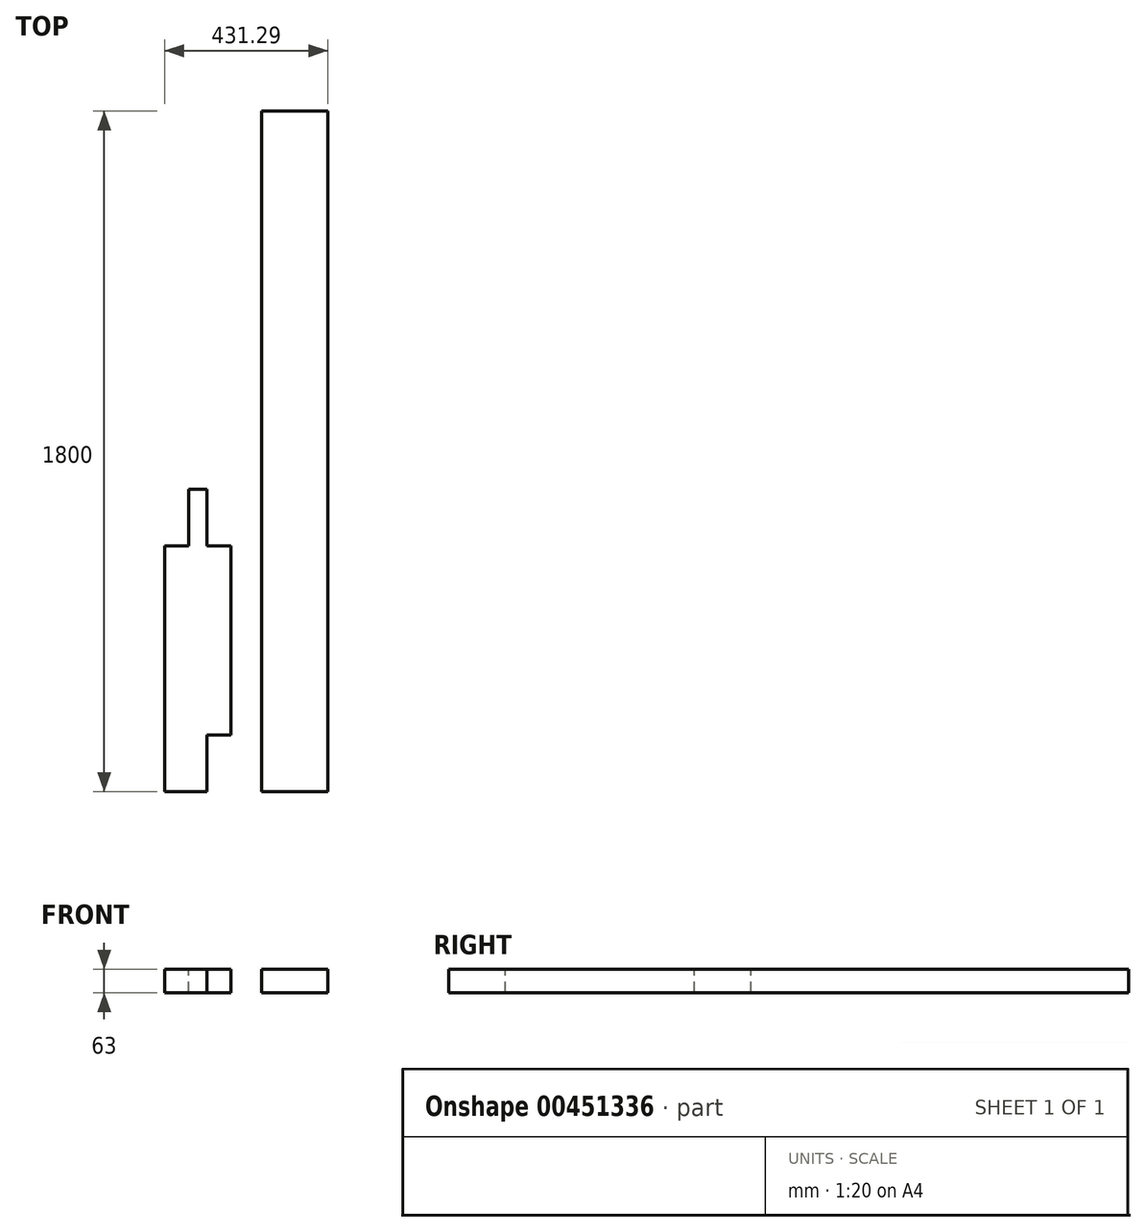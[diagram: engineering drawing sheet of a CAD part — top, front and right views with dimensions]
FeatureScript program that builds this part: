
annotation { "Feature Type Name" : "Feature", "Feature Type Description" : "" }
export const myFeature = defineFeature(function(context is Context, id is Id, definition is map)
    precondition{}
    {
        {
            var Q0;
            Q0=qCreatedBy(makeId("Front.planeOp"),FACE);
            var sketch = newSketch(context, id + "F0", { "sketchPlane" : qUnion([Q0])});
            skLineSegment(sketch, "E0.bottom", {"start": v(87.5, 31.5) * mm, "end": v(-87.5, 31.5) * mm});
            skLineSegment(sketch, "E0.top", {"start": v(87.5, -31.5) * mm, "end": v(-87.5, -31.5) * mm});
            skLineSegment(sketch, "E0.left", {"start": v(87.5, 31.5) * mm, "end": v(87.5, -31.5) * mm});
            skLineSegment(sketch, "E0.right", {"start": v(-87.5, 31.5) * mm, "end": v(-87.5, -31.5) * mm});
            skPoint(sketch, "E0.middle", {"position": v(0, 0) * mm});
            skSolve(sketch);
        }
        {
            var Q0;
            Q0 = qSketchRegion(id + "F0", true);
            extrude(context, id + "F1", {"entities" : qUnion([Q0]), "oppositeDirection" : true, "depth" : 800 * mm});
        }
        {
            var Q0;
            Q0=makeQuery(id+"F1.opExtrude","SWEPT_FACE",FACE,{"disambiguationData":[OSD([sQuery(id+"F0.wireOp",EDGE,"E0.bottom")])]});
            var sketch = newSketch(context, id + "F2", { "sketchPlane" : qUnion([Q0])});
            skLineSegment(sketch, "E1.bottom", {"start": v(87.5, 0) * mm, "end": v(24.5, 0) * mm});
            skLineSegment(sketch, "E1.top", {"start": v(87.5, 150) * mm, "end": v(24.5, 150) * mm});
            skLineSegment(sketch, "E1.left", {"start": v(87.5, 0) * mm, "end": v(87.5, 150) * mm});
            skLineSegment(sketch, "E1.right", {"start": v(24.5, 0) * mm, "end": v(24.5, 150) * mm});
            skLineSegment(sketch, "E2.bottom", {"start": v(-87.5, 800) * mm, "end": v(-24.5, 800) * mm});
            skLineSegment(sketch, "E2.top", {"start": v(-87.5, 650) * mm, "end": v(-24.5, 650) * mm});
            skLineSegment(sketch, "E2.left", {"start": v(-87.5, 800) * mm, "end": v(-87.5, 650) * mm});
            skLineSegment(sketch, "E2.right", {"start": v(-24.5, 800) * mm, "end": v(-24.5, 650) * mm});
            skLineSegment(sketch, "E3.bottom", {"start": v(87.5, 800) * mm, "end": v(24.5, 800) * mm});
            skLineSegment(sketch, "E3.top", {"start": v(87.5, 650) * mm, "end": v(24.5, 650) * mm});
            skLineSegment(sketch, "E3.left", {"start": v(87.5, 800) * mm, "end": v(87.5, 650) * mm});
            skLineSegment(sketch, "E3.right", {"start": v(24.5, 800) * mm, "end": v(24.5, 650) * mm});
            skSolve(sketch);
        }
        {
            var Q0;
            Q0 = qSketchRegion(id + "F2", true);
            extrude(context, id + "F3", {"entities" : qUnion([Q0]), "operationType" : NewBodyOperationType.REMOVE, "endBound" : BoundingType.THROUGH_ALL, "oppositeDirection" : true, "depth" : 25 * mm});
        }
        {
            var Q0;
            Q0=qCreatedBy(makeId("Front.planeOp"),FACE);
            var sketch = newSketch(context, id + "F4", { "sketchPlane" : qUnion([Q0])});
            skLineSegment(sketch, "E4.bottom", {"start": v(168.79, 31.5) * mm, "end": v(343.79, 31.5) * mm});
            skLineSegment(sketch, "E4.top", {"start": v(168.79, -31.5) * mm, "end": v(343.79, -31.5) * mm});
            skLineSegment(sketch, "E4.left", {"start": v(168.79, 31.5) * mm, "end": v(168.79, -31.5) * mm});
            skLineSegment(sketch, "E4.right", {"start": v(343.79, 31.5) * mm, "end": v(343.79, -31.5) * mm});
            skPoint(sketch, "E4.middle", {"position": v(256.29, 0) * mm});
            skSolve(sketch);
        }
        {
            var Q0;
            Q0=makeQuery(id+"F4.imprint","IMPRINT",FACE,{"disambiguationData":[TD([[makeQuery(id+"F4.imprint","IMPRINT",EDGE,{"derivedFrom":sQuery(id+"F4.wireOp",EDGE,"E4.bottom")}),-1.0]])]});
            extrude(context, id + "F5", {"entities" : qUnion([Q0]), "oppositeDirection" : true, "depth" : 1800 * mm});
        }
    });
